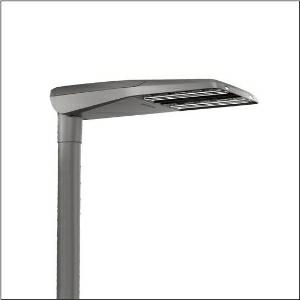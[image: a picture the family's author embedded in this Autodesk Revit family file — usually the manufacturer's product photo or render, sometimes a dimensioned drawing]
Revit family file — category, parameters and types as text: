
# Revit family: streetlight_sl_11_iq_midi___pc-r_5xc3f21f08me_be3f
name_source: partatom
category: Lighting Fixtures
units: mm (PartAtom-declared; Revit-internal decimal feet)

## family parameters
Cut with Voids When Loaded = No
Host = Face
Light Source = No
Part Type = Normal
Room Calculation Point = No
Round Connector Dimension = Use Diameter
Shared = No

## types (1)
- --- (1 x LED, 12740 lm, 124.7 W, 2200K)
    Apparent Load = 125 VA
    CIE Flux Codes = 37 73 96 100 100
    Color Rendering = 70
    Color Temperature = 2200K
    Default Elevation = 1800 mm
    Description = Streetlight SL 11 iQ midi, mast luminaire, primary light control with 3 zone facetted reflector, of plastic, silver coated, highly specular, primary optical cover: cover, of PMMA, transparent, light distribution: PC-R, light emission: direct distribution, primary light characteristic: asymmetric, installation type: post-top, side-entry, LED, High Power LED, rated luminous flux: 12.860lm, luminous efficacy: 103lm/W, light colour: 722, colour temperature: 2200K, control: Street-Remote, optimised constant luminous flux control (CLO 2.0), Desk-Remote (wireless, voltage-free reading and setting of iQ features in the workshop via application-optimized NFC function/RFID function), Light-Fading, Smart-Wire, Night-Set, Lumen-Switch, Temp-Guard, Auto-Match, with cable H07RN-F 5x 1.5mm², mains connection: 220..240V, AC, 50/60Hz, connection cable pre-assembled, cable length: 12,5m, start of lifetime: 125W, end of lifetime: 132W, reduction: 57W, luminaire housing, of diecast aluminium, powder-coated, Siteco® metallic grey (DB 702S), length: 780mm, width: 376mm, height: 118mm, spigot size: 60/76mm (post-top) and 42/60/76mm (side-entry), mast flange for spigot size: 42mm: 5XC10008XM4, 60mm: 5XC10008XM2, 76/60mm: 5XC10108XM1, equipment: Power, protection rating (complete): IP66, insulation class (complete): insulation class II (safety insulation), certification: CE, ENEC, VDE, impact resistance: IK09, permissible operating ambient temperature for outdoor applications: -25..+50°C, standard-compliant lighting for roads and squares, packaging unit: 1 piece

Light Distribution: PC-R
    Height = 118 mm
    Lamp = 1 x LED
    Lamp Light Flux = 12740 lm
    Lamp Power = 124.7 W
    Lamp count = 1
    Length = 780 mm
    Luminous efficacy = 102 lm/W
    Manufacturer = Siteco
    ModVariant = No
    Model = 5XC3F21F08ME
    Number of Poles = 1
    OnlyDefault = Yes
    Power Factor = 1
    Product Name = Streetlight SL 11 iQ midi | PC-R
    Product group = mast luminaire | pylon top
    ProductGroupID = 6100
    Protection Class = Protection class II
    Protection Degree = IP 66
    RLX_Detail_Level = 1
    RlxData = <blob elided: 74025 chars, md5=7cb49d1c>
    Socket = socket
    Standby Power = 0 W
    System Light Flux = 12741 lm
    System Power = 125 W
    Type Comments = factory setting: luminous flux: 100 % | dim-lin: 254 | 557 mA
    Type Image = l_1005960.jpg
    URL = http://relux.com
    VarID = @adj_036711
    Voltage = 0 V
    Weight = 0.00 kg
    Width = 376 mm

## geometry (parser evidence)
native form markers: Blend x4, Sweep x10
no freeform markers — native parametric forms only
